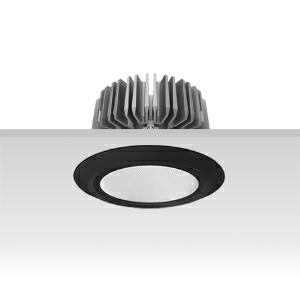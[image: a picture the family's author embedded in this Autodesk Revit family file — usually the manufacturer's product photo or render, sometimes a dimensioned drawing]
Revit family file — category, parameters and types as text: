
# Revit family: 3f_filippi_-_3f_reno_bianco_ampio_3f_filippi_-_30379_a01047_-_3f_reno_150_wh_2000-930_dali_wide___smp_bk_0920
name_source: partatom
category: Lighting Fixtures
units: mm (PartAtom-declared; Revit-internal decimal feet)

## family parameters
Cut with Voids When Loaded = No
Host = Face
Light Source = No
Part Type = Normal
Room Calculation Point = No
Round Connector Dimension = Use Diameter
Shared = No

## types (1)
- 3F Filippi - 3F Reno Bianco Ampio (1 x LED, 1652 lm, 24 W, 3000 K)
    Apparent Load = 24 VA
    Approval mark = CE
    CIE Flux Codes = 73 92 98 100 100
    Color Rendering = 90
    Color Temperature = 3000 K
    Control Gear = Electronic transformer
    Default Elevation = 1800 mm
    Description = ILLUMINOTECHNICAL
Luminous efficiency 100% (DLOR 100%, ULOR 0%).
Initial luminous flux of the luminaire 1652 lm.
Direct symmetric wide distribution.
Installation Interdistance Transv.D = 1.01 x hu - Long.D = 1.00 x hu.
Tabular UGR (CIE 117 - 4H-8H; S=0.25H; 70/50/20): RUG 23.3 - 23.3.
Beam angle: 70° - 70°.
Luminous efficacy 69 lm/W.
Lifetime (L90/B10): 30000 h. (tq+25°C)
Lifetime (L85/B10): 50000 h. (tq+25°C)
Lifetime (L70/B10): 80000 h. (tq+25°C)
Sudden decreased luminous flux after 50000 hours: 0% (C0).
Photobiological safety in compliance with IEC/TR 62778: RG0 risk exempt, (IEC 62471).
In compliance with IEC/EN 62722-2-1 - IEC/EN 62717 standards.

SOURCE
Compact LED module 2000/930.
Energy efficiency class (UE 2019/2020 - UE 2019/2015): E.
CIE 13.3 Colour rendering index: CRI >90 (R9 >50%).
IES TM-30 Fidelity Index: Rf = 92 Rg = 101.
CCT nominal colour temperature 3000 K.
Colour initial tolerance (MacAdam): SDCM 3.
Zhaga Book 3 compliant.

MECHANICAL
Passive heat dissipator in die-casting aluminium, oversized, for optimum thermal management of the LED module.
Parabolic element with graduated/concentric rings in white polycarbonate.
Transparent external lens with glossy and satin differentiated surfaces, with a cooling and anti-insect system in methacrylate (PMMA).
Fastening spring clips in stainless steel.
Dimensions: diameter 176 mm, height 111 mm. Weight 0.79 kg.
IP44 protection degree for exposed part, IP20 for recessed part.
Mechanical strength to impacts IK05 (0.7 joule).
Glow-wire test resistance 650°C.

ELECTRICAL
Wiring on a separate unit.
Halogen Free DALI-2 DATI (Parts 251, 252, 253), PUSH-DIM, electronic wiring 230V-50/60Hz, power factor 0.95 at full load, THD <25%, constant output current, SELV, class II, 1 driver, 1 DALI addresse.
Power of the luminaire 24 W.
ENEC - CE.
SAFE FLICKER: PstLM=<1 and SVM=<0.4 (IEC TR 61547-1 and IEC TR 63158), to ensure a more comfortable and safe light.
Luminaire compliant with EN 60598-2-22 for power supply from a centralised emergency system CPSS (Central Power Supply System), not incorporated in the luminaire - high risk areas excluded. The default power and flux are 100% in AC and 100% in DC.
Ambient temperature from 0°C to +25°C.
Temperature class T6 max 85°C.
Relative humidity UR: <85%.

INSTALLATION
Pull-up recessed fitting.
False ceiling carving: 150 mm.
All accessories dedicated to this product are available on the Catalog and on our website www.3F-Filippi.com.

ACCESSORIES
A01047 - Anti-glare microprismatic SMP diffuser in methacrylate (PMMA), locked and in line with the trim, in black polycarbonate.

APPLICATIONS
Suitable product for food production plants (HACCP), IFS (Food Version 6), BRC (GSFS Food Version 7).
Environments: architectural, commercial, exhibition areas, transit areas, corridors, shops, display windows, service areas.
In false ceilings with narrow voids.

LIGHT MANAGEMENT
Recommended minimum setting: 10%.
The luminaire, equipped with (DALI-2 DATI) driver, can be controlled manually with 3F Easy Dim technology or automatically/manually with wired or wireless DALI/D2D control systems.
The D2D driver guarantees interoperability with other devices with the same certification by making the following information available:
Device Data (Part 251), Energy Report (Part 252), Diagnosis & Maintenance (Part 253).
In electrical systems without a regulation system (manual or automatic) and DALI bus, a suitable jumper must be made on the DA-DA terminals of the appliance.

WARNING
Luminaire designed for disposal/recycling at end-of-life.
Replaceable (LED only) light source by a professional. Replaceable control gear by a professional.
    Height = 0 mm  [stored 0 ft]
    Lamp = 1 x LED
    Lamp Light Flux = 1652 lm
    Lamp Power = 24 W
    Lamp count = 1
    Length = 176 mm
    Lifetime = 50000 h
    Luminous efficacy = 69 lm/W
    Manufacturer = 3F Filippi
    ModVariant = No
    Model = 3F Filippi - 30379+A01047 - 3F Reno 150 WH 2000-930 DALI WIDE + SMP BK
    Mounting Place = Ceiling
    Mounting Type = Recessed
    Number of Poles = 1
    OnlyDefault = Yes
    Power Factor = 1
    Product Name = 3F Filippi - 3F Reno Bianco Ampio
    Product group = recessed luminaire
    ProductGroupID = 4
    Protection Class = Protection class II
    Protection Degree = IP 20
    RLX_Detail_Level = 1
    RLX_Emergency_Light_Flux = 0 lm
    RLX_Emergency_Type = 0
    RLX_Emergency_Type_DB = No
    RlxData = <blob elided: 88245 chars, md5=78e0e56c>
    Socket = socket
    Standby Power = 0 W
    System Light Flux = 1652 lm
    System Power = 24 W
    Type Comments = Product without accessories
    Type Image = 3ffilippi_3f_reno_150_bk_vs_smp.jpg
    URL = http://relux.com
    VarID = ---
    Voltage = 0 V
    Weight = 0.00 kg
    Width = 0 mm  [stored 0 ft]

note: [stored X ft] marks values corroborated as IEEE doubles in the binary element streams (Revit-internal decimal feet)

## geometry (parser evidence)
native form markers: Blend x4, Sweep x12
no freeform markers — native parametric forms only
